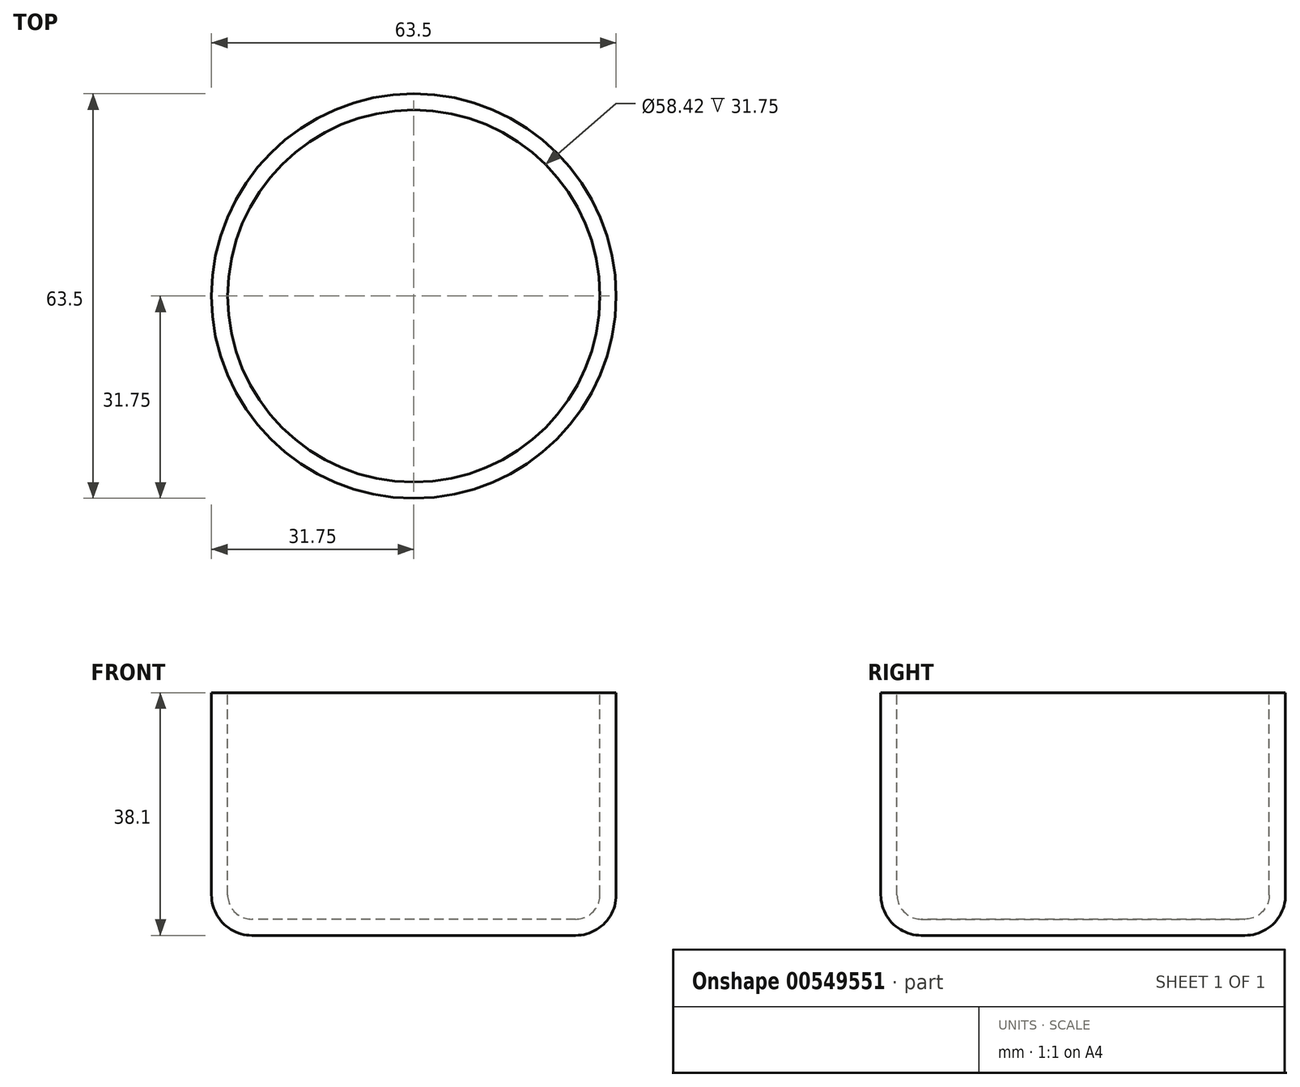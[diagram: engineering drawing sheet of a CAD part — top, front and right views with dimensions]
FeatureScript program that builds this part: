
annotation { "Feature Type Name" : "Feature", "Feature Type Description" : "" }
export const myFeature = defineFeature(function(context is Context, id is Id, definition is map)
    precondition{}
    {
        {
            var Q0;
            Q0=qCreatedBy(makeId("Front.planeOp"),FACE);
            var sketch = newSketch(context, id + "F0", { "sketchPlane" : qUnion([Q0])});
            skLineSegment(sketch, "E0", {"start": v(0, 41.5) * mm, "end": v(0, -55.04) * mm, "construction": true});
            skLineSegment(sketch, "E1.bottom", {"start": v(0, 0) * mm, "end": v(31.75, 0) * mm});
            skLineSegment(sketch, "E1.top", {"start": v(0, -38.1) * mm, "end": v(25.4, -38.1) * mm});
            skLineSegment(sketch, "E1.left", {"start": v(0, 0) * mm, "end": v(0, -38.1) * mm});
            skLineSegment(sketch, "E1.right", {"start": v(31.75, 0) * mm, "end": v(31.75, -31.75) * mm});
            skPoint(sketch, "E2.visualSharp", {"position": v(31.75, -38.1) * mm});
            skArc(sketch, "E2.filletArc", {"start": v(25.4, -38.1) * mm, "mid": v(29.9, -36.24) * mm, "end": v(31.75, -31.75) * mm});
            skSolve(sketch);
        }
        {
            var Q0;
            Q0 = qSketchRegion(id + "F0", true);
            var Q1;
            Q1=sQuery(id+"F0.wireOp",EDGE,"E0");
            revolve(context, id + "F1", {"entities" : qUnion([Q0]), "axis" : qUnion([Q1]), "revolveType" : RevolveType.FULL});
        }
        {
            var Q0;
            Q0=makeQuery(id+"F1.opRevolve","SWEPT_FACE",FACE,{"disambiguationData":[OSD([sQuery(id+"F0.wireOp",EDGE,"E1.bottom")])]});
            shell(context, id + "F2", {"entities" : qUnion([Q0]), "thickness" : 2.54 * mm});
        }
    });
